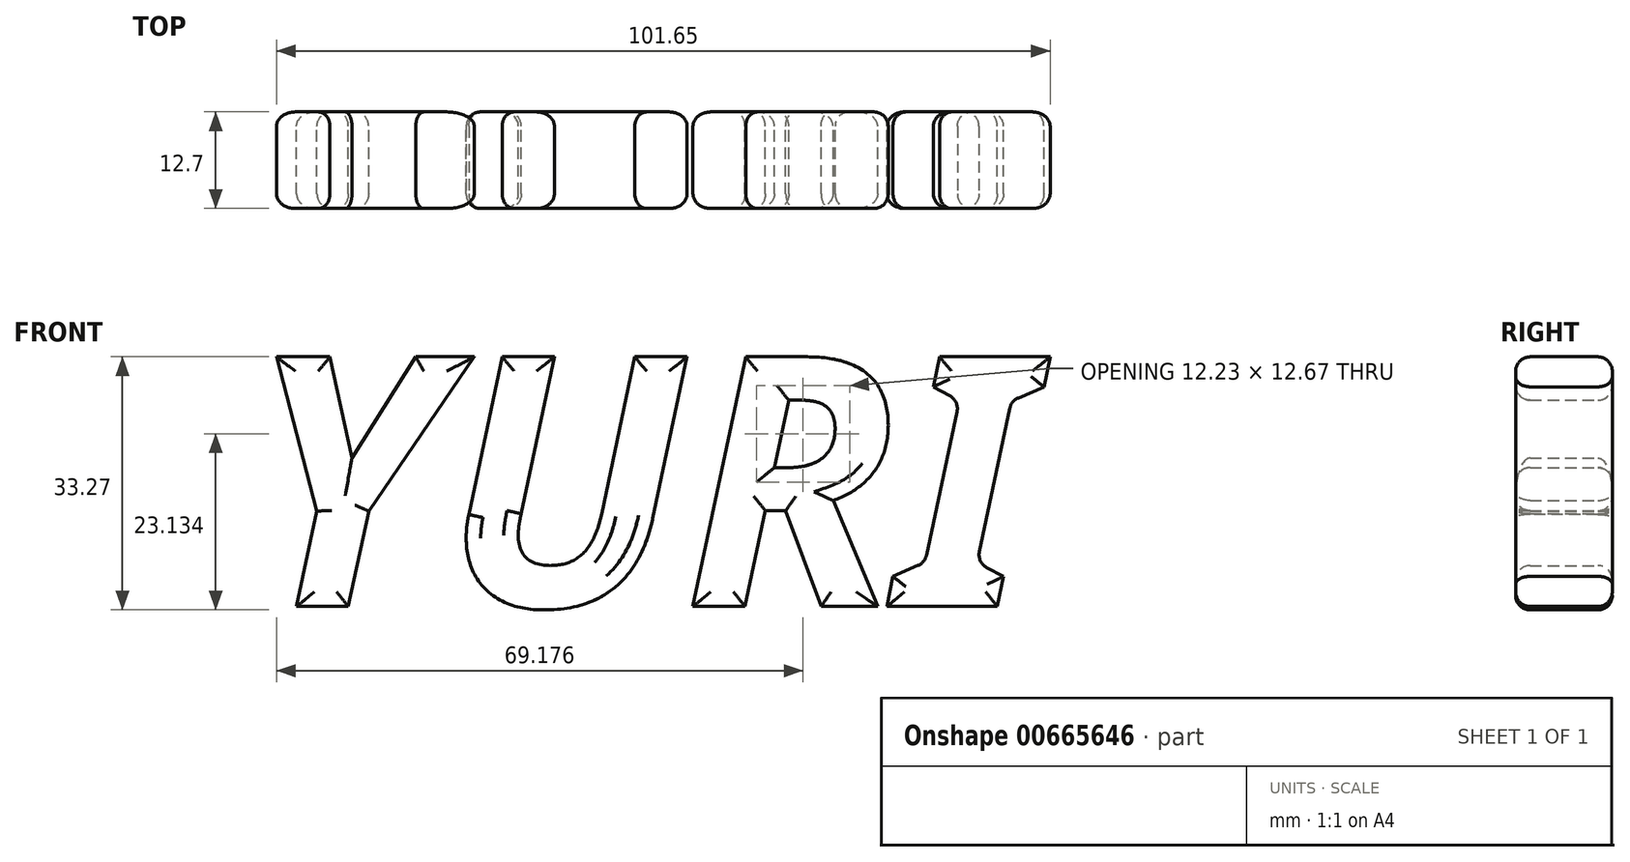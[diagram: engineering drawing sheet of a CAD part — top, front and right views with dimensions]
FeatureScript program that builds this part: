
annotation { "Feature Type Name" : "Feature", "Feature Type Description" : "" }
export const myFeature = defineFeature(function(context is Context, id is Id, definition is map)
    precondition{}
    {
        {
            var Q0;
            Q0=qCreatedBy(makeId("Front.planeOp"),FACE);
            var sketch = newSketch(context, id + "F0", { "sketchPlane" : qUnion([Q0])});
            skText(sketch, "E0", { "text": "YURI", "fontName": "NotoSans-BoldItalic.ttf"});
            const initialGuessF0  = {"E0": [0, 0, 1, 0, 0.0331]};
            skSetInitialGuess(sketch, initialGuessF0);
            skSolve(sketch);
        }
        {
            var Q0;
            Q0 = qSketchRegion(id + "F0", true);
            extrude(context, id + "F1", {"entities" : qUnion([Q0]), "depth" : 12.7 * mm, "offsetDistance" : 25.4 * mm});
        }
        {
            var Q0;
            Q0=makeQuery(id+"F1.opExtrude","CAP_FACE",FACE,{"disambiguationData":[OSD([sQuery(id+"F0.wireOp",EDGE,"E0.sketch_text.stroke-0"),sQuery(id+"F0.wireOp",EDGE,"E0.sketch_text.stroke-1"),sQuery(id+"F0.wireOp",EDGE,"E0.sketch_text.stroke-2"),sQuery(id+"F0.wireOp",EDGE,"E0.sketch_text.stroke-3"),sQuery(id+"F0.wireOp",EDGE,"E0.sketch_text.stroke-4"),sQuery(id+"F0.wireOp",EDGE,"E0.sketch_text.stroke-5"),sQuery(id+"F0.wireOp",EDGE,"E0.sketch_text.stroke-6"),sQuery(id+"F0.wireOp",EDGE,"E0.sketch_text.stroke-7"),sQuery(id+"F0.wireOp",EDGE,"E0.sketch_text.stroke-8")])],"isStart":false});
            var Q1;
            Q1=makeQuery(id+"F1.opExtrude","CAP_FACE",FACE,{"disambiguationData":[OSD([sQuery(id+"F0.wireOp",EDGE,"E0.sketch_text.stroke-0"),sQuery(id+"F0.wireOp",EDGE,"E0.sketch_text.stroke-1"),sQuery(id+"F0.wireOp",EDGE,"E0.sketch_text.stroke-2"),sQuery(id+"F0.wireOp",EDGE,"E0.sketch_text.stroke-3"),sQuery(id+"F0.wireOp",EDGE,"E0.sketch_text.stroke-4"),sQuery(id+"F0.wireOp",EDGE,"E0.sketch_text.stroke-5"),sQuery(id+"F0.wireOp",EDGE,"E0.sketch_text.stroke-6"),sQuery(id+"F0.wireOp",EDGE,"E0.sketch_text.stroke-7"),sQuery(id+"F0.wireOp",EDGE,"E0.sketch_text.stroke-8")])],"isStart":true});
            var Q2;
            Q2=makeQuery(id+"F1.opExtrude","CAP_FACE",FACE,{"disambiguationData":[OSD([sQuery(id+"F0.wireOp",EDGE,"E0.sketch_text.stroke-9"),sQuery(id+"F0.wireOp",EDGE,"E0.sketch_text.stroke-10"),sQuery(id+"F0.wireOp",EDGE,"E0.sketch_text.stroke-11"),sQuery(id+"F0.wireOp",EDGE,"E0.sketch_text.stroke-12"),sQuery(id+"F0.wireOp",EDGE,"E0.sketch_text.stroke-13"),sQuery(id+"F0.wireOp",EDGE,"E0.sketch_text.stroke-14"),sQuery(id+"F0.wireOp",EDGE,"E0.sketch_text.stroke-15"),sQuery(id+"F0.wireOp",EDGE,"E0.sketch_text.stroke-16"),sQuery(id+"F0.wireOp",EDGE,"E0.sketch_text.stroke-17"),sQuery(id+"F0.wireOp",EDGE,"E0.sketch_text.stroke-18"),sQuery(id+"F0.wireOp",EDGE,"E0.sketch_text.stroke-19"),sQuery(id+"F0.wireOp",EDGE,"E0.sketch_text.stroke-20"),sQuery(id+"F0.wireOp",EDGE,"E0.sketch_text.stroke-21"),sQuery(id+"F0.wireOp",EDGE,"E0.sketch_text.stroke-22"),sQuery(id+"F0.wireOp",EDGE,"E0.sketch_text.stroke-23")])],"isStart":false});
            var Q3;
            Q3=makeQuery(id+"F1.opExtrude","CAP_FACE",FACE,{"disambiguationData":[OSD([sQuery(id+"F0.wireOp",EDGE,"E0.sketch_text.stroke-9"),sQuery(id+"F0.wireOp",EDGE,"E0.sketch_text.stroke-10"),sQuery(id+"F0.wireOp",EDGE,"E0.sketch_text.stroke-11"),sQuery(id+"F0.wireOp",EDGE,"E0.sketch_text.stroke-12"),sQuery(id+"F0.wireOp",EDGE,"E0.sketch_text.stroke-13"),sQuery(id+"F0.wireOp",EDGE,"E0.sketch_text.stroke-14"),sQuery(id+"F0.wireOp",EDGE,"E0.sketch_text.stroke-15"),sQuery(id+"F0.wireOp",EDGE,"E0.sketch_text.stroke-16"),sQuery(id+"F0.wireOp",EDGE,"E0.sketch_text.stroke-17"),sQuery(id+"F0.wireOp",EDGE,"E0.sketch_text.stroke-18"),sQuery(id+"F0.wireOp",EDGE,"E0.sketch_text.stroke-19"),sQuery(id+"F0.wireOp",EDGE,"E0.sketch_text.stroke-20"),sQuery(id+"F0.wireOp",EDGE,"E0.sketch_text.stroke-21"),sQuery(id+"F0.wireOp",EDGE,"E0.sketch_text.stroke-22"),sQuery(id+"F0.wireOp",EDGE,"E0.sketch_text.stroke-23")])],"isStart":true});
            var Q4;
            Q4=makeQuery(id+"F1.opExtrude","CAP_FACE",FACE,{"disambiguationData":[OSD([sQuery(id+"F0.wireOp",EDGE,"E0.sketch_text.stroke-43"),sQuery(id+"F0.wireOp",EDGE,"E0.sketch_text.stroke-44"),sQuery(id+"F0.wireOp",EDGE,"E0.sketch_text.stroke-45"),sQuery(id+"F0.wireOp",EDGE,"E0.sketch_text.stroke-46"),sQuery(id+"F0.wireOp",EDGE,"E0.sketch_text.stroke-47"),sQuery(id+"F0.wireOp",EDGE,"E0.sketch_text.stroke-48"),sQuery(id+"F0.wireOp",EDGE,"E0.sketch_text.stroke-49"),sQuery(id+"F0.wireOp",EDGE,"E0.sketch_text.stroke-50"),sQuery(id+"F0.wireOp",EDGE,"E0.sketch_text.stroke-51"),sQuery(id+"F0.wireOp",EDGE,"E0.sketch_text.stroke-52"),sQuery(id+"F0.wireOp",EDGE,"E0.sketch_text.stroke-53"),sQuery(id+"F0.wireOp",EDGE,"E0.sketch_text.stroke-54")])],"isStart":true});
            var Q5;
            Q5=makeQuery(id+"F1.opExtrude","CAP_FACE",FACE,{"disambiguationData":[OSD([sQuery(id+"F0.wireOp",EDGE,"E0.sketch_text.stroke-24"),sQuery(id+"F0.wireOp",EDGE,"E0.sketch_text.stroke-25"),sQuery(id+"F0.wireOp",EDGE,"E0.sketch_text.stroke-26"),sQuery(id+"F0.wireOp",EDGE,"E0.sketch_text.stroke-27"),sQuery(id+"F0.wireOp",EDGE,"E0.sketch_text.stroke-28"),sQuery(id+"F0.wireOp",EDGE,"E0.sketch_text.stroke-29"),sQuery(id+"F0.wireOp",EDGE,"E0.sketch_text.stroke-30"),sQuery(id+"F0.wireOp",EDGE,"E0.sketch_text.stroke-31"),sQuery(id+"F0.wireOp",EDGE,"E0.sketch_text.stroke-32"),sQuery(id+"F0.wireOp",EDGE,"E0.sketch_text.stroke-33"),sQuery(id+"F0.wireOp",EDGE,"E0.sketch_text.stroke-34"),sQuery(id+"F0.wireOp",EDGE,"E0.sketch_text.stroke-35"),sQuery(id+"F0.wireOp",EDGE,"E0.sketch_text.stroke-36"),sQuery(id+"F0.wireOp",EDGE,"E0.sketch_text.stroke-37"),sQuery(id+"F0.wireOp",EDGE,"E0.sketch_text.stroke-38"),sQuery(id+"F0.wireOp",EDGE,"E0.sketch_text.stroke-39"),sQuery(id+"F0.wireOp",EDGE,"E0.sketch_text.stroke-40"),sQuery(id+"F0.wireOp",EDGE,"E0.sketch_text.stroke-41"),sQuery(id+"F0.wireOp",EDGE,"E0.sketch_text.stroke-42")])],"isStart":true});
            var Q6;
            Q6=makeQuery(id+"F1.opExtrude","CAP_FACE",FACE,{"disambiguationData":[OSD([sQuery(id+"F0.wireOp",EDGE,"E0.sketch_text.stroke-24"),sQuery(id+"F0.wireOp",EDGE,"E0.sketch_text.stroke-25"),sQuery(id+"F0.wireOp",EDGE,"E0.sketch_text.stroke-26"),sQuery(id+"F0.wireOp",EDGE,"E0.sketch_text.stroke-27"),sQuery(id+"F0.wireOp",EDGE,"E0.sketch_text.stroke-28"),sQuery(id+"F0.wireOp",EDGE,"E0.sketch_text.stroke-29"),sQuery(id+"F0.wireOp",EDGE,"E0.sketch_text.stroke-30"),sQuery(id+"F0.wireOp",EDGE,"E0.sketch_text.stroke-31"),sQuery(id+"F0.wireOp",EDGE,"E0.sketch_text.stroke-32"),sQuery(id+"F0.wireOp",EDGE,"E0.sketch_text.stroke-33"),sQuery(id+"F0.wireOp",EDGE,"E0.sketch_text.stroke-34"),sQuery(id+"F0.wireOp",EDGE,"E0.sketch_text.stroke-35"),sQuery(id+"F0.wireOp",EDGE,"E0.sketch_text.stroke-36"),sQuery(id+"F0.wireOp",EDGE,"E0.sketch_text.stroke-37"),sQuery(id+"F0.wireOp",EDGE,"E0.sketch_text.stroke-38"),sQuery(id+"F0.wireOp",EDGE,"E0.sketch_text.stroke-39"),sQuery(id+"F0.wireOp",EDGE,"E0.sketch_text.stroke-40"),sQuery(id+"F0.wireOp",EDGE,"E0.sketch_text.stroke-41"),sQuery(id+"F0.wireOp",EDGE,"E0.sketch_text.stroke-42")])],"isStart":false});
            var Q7;
            Q7=makeQuery(id+"F1.opExtrude","CAP_FACE",FACE,{"disambiguationData":[OSD([sQuery(id+"F0.wireOp",EDGE,"E0.sketch_text.stroke-43"),sQuery(id+"F0.wireOp",EDGE,"E0.sketch_text.stroke-44"),sQuery(id+"F0.wireOp",EDGE,"E0.sketch_text.stroke-45"),sQuery(id+"F0.wireOp",EDGE,"E0.sketch_text.stroke-46"),sQuery(id+"F0.wireOp",EDGE,"E0.sketch_text.stroke-47"),sQuery(id+"F0.wireOp",EDGE,"E0.sketch_text.stroke-48"),sQuery(id+"F0.wireOp",EDGE,"E0.sketch_text.stroke-49"),sQuery(id+"F0.wireOp",EDGE,"E0.sketch_text.stroke-50"),sQuery(id+"F0.wireOp",EDGE,"E0.sketch_text.stroke-51"),sQuery(id+"F0.wireOp",EDGE,"E0.sketch_text.stroke-52"),sQuery(id+"F0.wireOp",EDGE,"E0.sketch_text.stroke-53"),sQuery(id+"F0.wireOp",EDGE,"E0.sketch_text.stroke-54")])],"isStart":false});
            var Q8;
            Q8=makeQuery(id+"F1.opExtrude","SWEPT_FACE",FACE,{"disambiguationData":[OSD([sQuery(id+"F0.wireOp",EDGE,"E0.sketch_text.stroke-46")])]});
            var Q9;
            Q9=makeQuery(id+"F1.opExtrude","SWEPT_FACE",FACE,{"disambiguationData":[OSD([sQuery(id+"F0.wireOp",EDGE,"E0.sketch_text.stroke-52")])]});
            fillet(context, id + "F2", {"entities" : qUnion([Q0, Q1, Q2, Q3, Q4, Q5, Q6, Q7, Q8, Q9]), "radius" : 1.9 * mm, "tangentPropagation" : true, "allowEdgeOverflow" : false});
        }
    });
